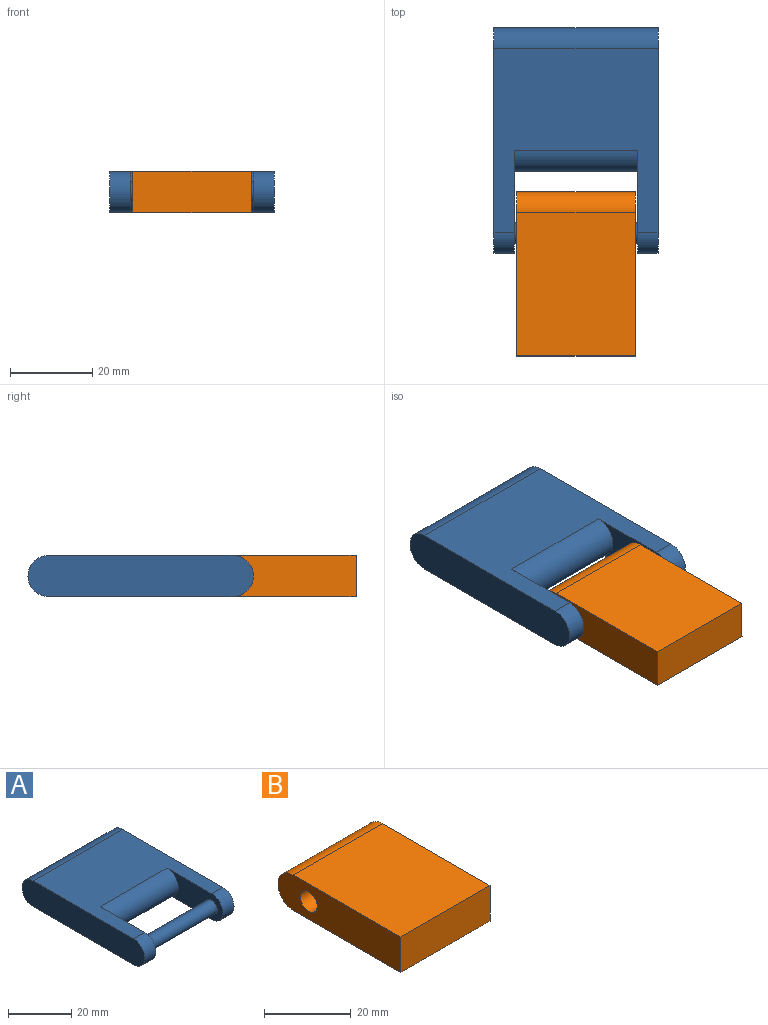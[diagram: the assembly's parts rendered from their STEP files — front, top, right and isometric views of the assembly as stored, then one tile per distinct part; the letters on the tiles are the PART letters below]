
ASSEMBLY  parts=2 mates=1
PART A: 11 faces, bbox 40x55x10 mm
  f0: plane 25x10mm, normal (-1,0,0), area 180.4mm2, adj f4,f5,f8,f9,f10
  f1: plane 55x10mm, normal (1,0,0), area 528.5mm2, adj f4,f5,f7,f8
  f2: plane 55x10mm, normal (-1,0,0), area 528.5mm2, adj f4,f5,f6,f7
  f3: plane 25x10mm, normal (1,0,0), area 180.4mm2, adj f4,f5,f6,f9,f10
  f4: plane 45x40mm, normal (0,0,1), area 1200mm2, adj f0,f1,f2,f3,f6,f7,f8,f9
  f5: plane 45x40mm, normal (0,0,-1), area 1200mm2, adj f0,f1,f2,f3,f6,f7,f8,f9
  f6: cylinder r=5mm len=10mm, axis (-1,0,0), area 78.5mm2, adj f2,f3,f4,f5
  f7: cylinder r=5mm len=40mm, axis (1,0,0), area 628.3mm2, adj f1,f2,f4,f5
  f8: cylinder r=5mm len=10mm, axis (-1,0,0), area 78.5mm2, adj f0,f1,f4,f5
  f9: cylinder r=5mm len=30mm, axis (-1,0,0), area 471.2mm2, adj f0,f3,f4,f5
  f10: cylinder r=2.5mm len=30mm, axis (-1,0,0), area 471.2mm2, adj f0,f3
PART B: 7 faces, bbox 29x40x10 mm
  f0: plane 40x10mm, normal (-1,0,0), area 365.5mm2, adj f1,f3,f4,f5,f6
  f1: plane 29x10mm, normal (0,-1,0), area 290mm2, adj f0,f2,f3,f4
  f2: plane 40x10mm, normal (1,0,0), area 365.5mm2, adj f1,f3,f4,f5,f6
  f3: plane 35x29mm, normal (0,0,1), area 1015mm2, adj f0,f1,f2,f6
  f4: plane 35x29mm, normal (0,0,-1), area 1015mm2, adj f0,f1,f2,f6
  f5: cylinder r=2.75mm len=29mm, axis (-1,0,0), area 501.1mm2, adj f0,f2
  f6: cylinder r=5mm len=29mm, axis (1,0,0), area 455.5mm2, adj f0,f2,f3,f4
PLACE A t=(-66.07,-23.31,49.05)mm
PLACE B rot(axis=(-1,0,0),0deg) t=(-66.07,-23.31,49.05)mm
MATE revolute A.f6 <-> B.f5  axis (-1,0,0) through (-46.07,-18.31,49.05)mm
